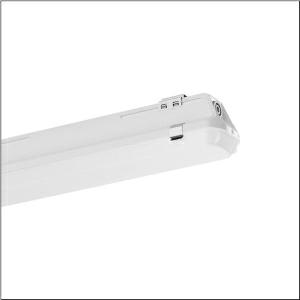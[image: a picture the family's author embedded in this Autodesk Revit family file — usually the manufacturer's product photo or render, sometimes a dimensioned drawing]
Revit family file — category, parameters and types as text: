
# Revit family: monsun_r__21_51fb207p460b_df7e
name_source: partatom
category: Lighting Fixtures
units: mm (PartAtom-declared; Revit-internal decimal feet)

## family parameters
Cut with Voids When Loaded = No
Host = Face
Light Source = No
Part Type = Normal
Room Calculation Point = No
Round Connector Dimension = Use Diameter
Shared = No

## types (1)
- Monsun® 21 (1 x LED, 5400 lm, 38 W, 4000K)
    Apparent Load = 38 VA
    CIE Flux Codes = 45 75 93 94 100
    Color Rendering = 80
    Color Temperature = 4000K
    Default Elevation = 1800 mm
    Description = Monsun® 21, damp-proof luminaire, chain hanger, primary optical cover: enclosure, of PC, light emission: direct distribution, primary light characteristic: symmetric, installation type: suspended mounting, surface-mounted, horizontal mounting, vertical mounting, LED, rated luminous flux: 5.400lm, luminous efficacy: 142lm/W, light colour: 840, colour temperature: 4000K, control gear: ECG, with terminal, 3-pole, max. 2.5mm², mains connection: 220..240V, AC, 50/60Hz, rated input power: 38W, housing, of glass-fibre reinforced polyester, uncoated, bright grey, incl. chain hanger, length: 1.590mm, width: 90mm, height: 88mm, clip for enclosure, of stainless steel (V2A), ceiling mounting element, of stainless steel (V2A), chain hanger, of stainless steel (V2A), protection rating (complete): IP66, insulation class (complete): insulation class I (protective earthing), certification: CE, ENEC, VDE, UKCA, protection symbol: D, impact resistance: IK08, permissible operating ambient temperature: -25..+35°C, standard: EN 50419, EN 60598-2-1, corresponds to IFS (International Featured Standards) requirements for safety and quality in the food industry, for indoor or canopied outdoor use, no direct snow, no direct sun, no direct rain, contact your sales advisor before using the luminaires in applications with unclear chemical exposure, large temperature fluctuations or condensation-forming humidity, LABS conformity tested according to VDMA 24364:2018-05, packaging unit: 1 piece
    Height = 89 mm
    Lamp = 1 x LED
    Lamp Light Flux = 5400 lm
    Lamp Power = 38 W
    Lamp count = 1
    Length = 1590 mm
    Luminous efficacy = 142 lm/W
    Manufacturer = Siteco
    ModVariant = No
    Model = 51FB207P460B
    Mounting Place = Ceiling
    Mounting Type = Surface mounted
    Number of Poles = 1
    OnlyDefault = Yes
    Power Factor = 1
    Product Name = Monsun® 21
    Product group = damp-proof luminaire
    ProductGroupID = 300
    Protection Class = Protection class I
    Protection Degree = IP 66
    RLX_Detail_Level = 1
    RLX_Emergency_Light_Flux = 0 lm
    RLX_Emergency_Type = 0
    RLX_Emergency_Type_DB = No
    RlxData = <blob elided: 88289 chars, md5=aa325934>
    Socket = socket
    Standby Power = 0 W
    System Light Flux = 5400 lm
    System Power = 38 W
    Type Comments = Product without accessories
    Type Image = l_1006717.jpg
    URL = http://relux.com
    VarID = ---
    Voltage = 0 V
    Weight = 0.00 kg
    Width = 90 mm

## geometry (parser evidence)
native form markers: Blend x4, Sweep x14
no freeform markers — native parametric forms only
